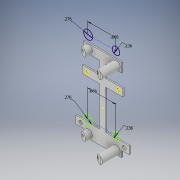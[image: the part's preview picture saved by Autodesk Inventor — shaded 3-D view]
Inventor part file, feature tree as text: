
AUTODESK INVENTOR PART (.ipt)
format: ipt  version: 2018 (Build 220112000, 112)  size: 322,048 bytes
history: native  units: in
note: dims shown in document units (in); Inventor stores cm internally (conversion verified against a paired STEP export)
features: extrude x13, sketch x9
ambient origin geometry x8: Origin, YZ Plane, XZ Plane, XY Plane, X Axis, Y Axis, Z Axis, Center Point
bodies: Solid1 (feature_tree)
feature tree (22):
  extrude  "Extrusion1"  Depth=1.2598in
  extrude  "Extrusion2"  TaperAngle=0.0deg  [1 undecoded]
  extrude  "Extrusion3"  Depth=0.2362in
  extrude  "Extrusion5"  Depth=0.0394in TaperAngle=0.0deg
  extrude  "Extrusion6"  Depth=0.6791in
  extrude  "Extrusion9"  Depth=0.1181in
  extrude  "Extrusion14"  Depth=0.1181in
  extrude  "Extrusion16"  Depth=0.4823in
  extrude  "Extrusion11"  Depth=0.1181in
  extrude  "Extrusion12"  Depth=0.1181in TaperAngle=0.0deg
  extrude  "Extrusion13"  Depth=2.2835in
  extrude  "Extrusion15"  TaperAngle=0.0deg  [1 undecoded]
  extrude  "Extrusion18"  TaperAngle=0.0deg  [1 undecoded]
  sketch  "Sketch1"  dims[d0=0.1969in d2=1.2598in]
  sketch  "Sketch2"  dims[d3=0.2362in d4=0.0in]
  sketch  "Sketch4"  dims[d5=1.6535in d6=0.2362in]
  sketch  "Sketch6"  dims[d7=0.0in d8=0.0394in d9=0.0in]
  sketch  "Sketch9"  dims[d10=1.3583in d13=0.6791in]
  sketch  "Sketch10"  dims[d14=0.6791in d15=0.1181in]
  sketch  "Sketch12"  dims[d16=0.1181in d17=0.9646in]
  sketch  "Sketch13"  dims[d18=0.4823in d19=0.4823in]
  sketch  "Sketch15"  dims[d20=0.1181in d21=0.1181in d22=0.0787in d23=0.0in d28=2.2835in d30=0.0in d31=0.0in d32=0.1969in d33=1.1811in d34=1.1811in d35=0.2756in d36=0.2756in d37=0.0787in d38=0.0787in d39=0.0787in d40=0.0787in d41=0.9055in d42=0.9055in d43=0.4528in d44=0.4528in d45=0.4528in d46=0.4528in d47=0.0394in d48=0.0in d52=0.2756in d55=0.2756in d57=0.0787in d58=0.0in d59=0.2362in d60=0.2362in d61=0.2362in d62=0.2362in d63=0.0787in d64=0.0in d65=1.4567in d66=1.4567in d72=0.4604in d73=0.25in d74=0.0in d77=5.0in d78=0.0in d79=0.0394in d80=0.0in d81=0.9055in d82=2.2835in d83=0.1293in d84=0.1293in d85=0.1893in d86=0.1893in d87=0.0787in d88=0.0787in d89=0.0787in d90=0.0787in d91=0.1181in d92=0.0in d97=0.2362in d98=0.8661in d99=0.2362in d100=0.8661in d101=0.4724in d102=0.0in d103=0.0787in d104=0.0787in d105=0.9075in d106=0.1969in d110=0.0787in d111=0.0787in d112=0.9075in d113=0.1969in d114=0.1969in d115=0.0in d116=1.378in d117=0.2362in d118=0.2362in d119=0.2362in d120=0.2362in d121=0.8661in d122=0.8661in d123=0.4331in d124=0.4331in d125=0.4331in d126=0.4331in d127=0.5512in d128=0.0in d139=0.0154in d140=0.5906in d141=0.4604in d142=0.9075in d143=0.0787in d144=0.0787in d145=0.0787in d146=0.9075in d147=0.0787in d148=0.0787in d149=0.0787in d150=0.1181in d151=0.0in]
note: 3 required parameter values undecoded (feature->parameter linkage not recoverable at this tier; creation-order binding heuristic only, values carry confidence <= 0.55)
